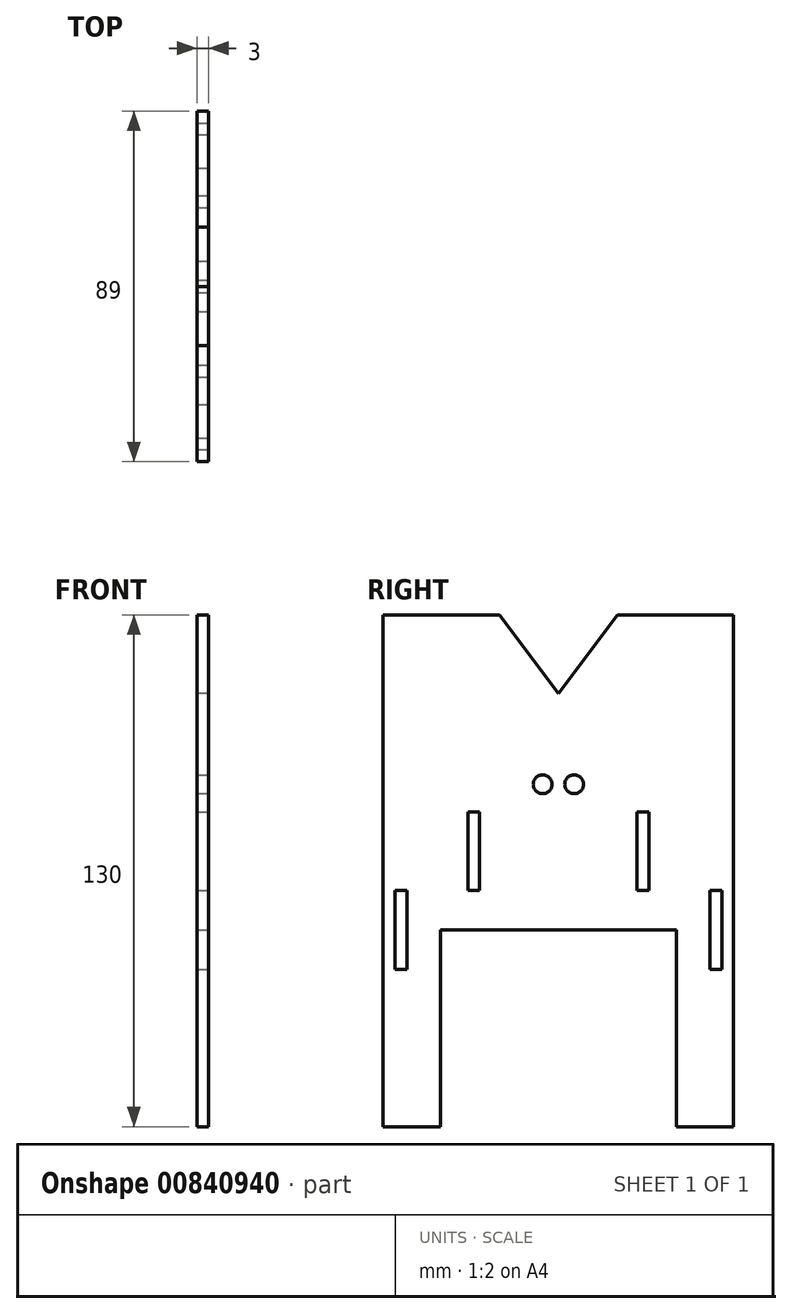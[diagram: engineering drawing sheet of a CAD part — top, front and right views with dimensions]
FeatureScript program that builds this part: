
annotation { "Feature Type Name" : "Feature", "Feature Type Description" : "" }
export const myFeature = defineFeature(function(context is Context, id is Id, definition is map)
    precondition{}
    {
        {
            var Q0;
            Q0=qCreatedBy(makeId("Right.planeOp"),FACE);
            var sketch = newSketch(context, id + "F0", { "sketchPlane" : qUnion([Q0])});
            skLineSegment(sketch, "E0", {"start": v(0, 130) * mm, "end": v(29.5, 130) * mm});
            skLineSegment(sketch, "E1", {"start": v(29.5, 130) * mm, "end": v(44.5, 110) * mm});
            skLineSegment(sketch, "E2", {"start": v(44.5, 110) * mm, "end": v(59.5, 130) * mm});
            skLineSegment(sketch, "E3", {"start": v(59.5, 130) * mm, "end": v(89, 130) * mm});
            skLineSegment(sketch, "E4", {"start": v(89, 130) * mm, "end": v(89, 0) * mm});
            skLineSegment(sketch, "E5", {"start": v(89, 0) * mm, "end": v(0, 0) * mm});
            skLineSegment(sketch, "E6", {"start": v(0, 0) * mm, "end": v(0, 130) * mm});
            skSolve(sketch);
        }
        {
            var Q0;
            Q0 = qSketchRegion(id + "F0", true);
            extrude(context, id + "F1", {"entities" : qUnion([Q0]), "depth" : 3 * mm, "offsetDistance" : 25 * mm});
        }
        {
            var Q0;
            Q0=makeQuery(id+"F1.opExtrude","CAP_FACE",FACE,{"disambiguationData":[OSD([sQuery(id+"F0.wireOp",EDGE,"E0"),sQuery(id+"F0.wireOp",EDGE,"E1"),sQuery(id+"F0.wireOp",EDGE,"E2"),sQuery(id+"F0.wireOp",EDGE,"E3"),sQuery(id+"F0.wireOp",EDGE,"E4"),sQuery(id+"F0.wireOp",EDGE,"E5"),sQuery(id+"F0.wireOp",EDGE,"E6")])],"isStart":false});
            var sketch = newSketch(context, id + "F2", { "sketchPlane" : qUnion([Q0])});
            skLineSegment(sketch, "E7.bottom", {"start": v(3, 60) * mm, "end": v(6, 60) * mm});
            skLineSegment(sketch, "E7.top", {"start": v(3, 40) * mm, "end": v(6, 40) * mm});
            skLineSegment(sketch, "E7.left", {"start": v(3, 60) * mm, "end": v(3, 40) * mm});
            skLineSegment(sketch, "E7.right", {"start": v(6, 60) * mm, "end": v(6, 40) * mm});
            skLineSegment(sketch, "E8", {"start": v(44.5, 110) * mm, "end": v(44.5, 73.4) * mm, "construction": true});
            skLineSegment(sketch, "E9.MirrorCS", {"start": v(83, 60) * mm, "end": v(83, 40) * mm});
            skLineSegment(sketch, "E10.MirrorCS", {"start": v(86, 60) * mm, "end": v(83, 60) * mm});
            skLineSegment(sketch, "E11.MirrorCS", {"start": v(86, 40) * mm, "end": v(83, 40) * mm});
            skLineSegment(sketch, "E12.MirrorCS", {"start": v(86, 60) * mm, "end": v(86, 40) * mm});
            skCircle(sketch, "E13", {"center": v(40.5, 87) * mm, "radius": 2.4 * mm});
            skCircle(sketch, "E14.MirrorC", {"center": v(48.5, 87) * mm, "radius": 2.4 * mm});
            skLineSegment(sketch, "E15.bottom", {"start": v(21.5, 80) * mm, "end": v(24.5, 80) * mm});
            skLineSegment(sketch, "E15.top", {"start": v(21.5, 60) * mm, "end": v(24.5, 60) * mm});
            skLineSegment(sketch, "E15.left", {"start": v(21.5, 80) * mm, "end": v(21.5, 60) * mm});
            skLineSegment(sketch, "E15.right", {"start": v(24.5, 80) * mm, "end": v(24.5, 60) * mm});
            skLineSegment(sketch, "E16.MirrorCS", {"start": v(67.5, 80) * mm, "end": v(64.5, 80) * mm});
            skLineSegment(sketch, "E17.MirrorCS", {"start": v(67.5, 60) * mm, "end": v(64.5, 60) * mm});
            skLineSegment(sketch, "E18.MirrorCS", {"start": v(64.5, 80) * mm, "end": v(64.5, 60) * mm});
            skLineSegment(sketch, "E19.MirrorCS", {"start": v(67.5, 80) * mm, "end": v(67.5, 60) * mm});
            skLineSegment(sketch, "E20.bottom", {"start": v(14.5, 0) * mm, "end": v(74.5, 0) * mm});
            skLineSegment(sketch, "E20.top", {"start": v(14.5, 50) * mm, "end": v(74.5, 50) * mm});
            skLineSegment(sketch, "E20.left", {"start": v(14.5, 0) * mm, "end": v(14.5, 50) * mm});
            skLineSegment(sketch, "E20.right", {"start": v(74.5, 0) * mm, "end": v(74.5, 50) * mm});
            skSolve(sketch);
        }
        {
            var Q0;
            Q0 = qSketchRegion(id + "F2", true);
            extrude(context, id + "F3", {"entities" : qUnion([Q0]), "operationType" : NewBodyOperationType.REMOVE, "oppositeDirection" : true, "depth" : 25 * mm, "offsetDistance" : 25 * mm});
        }
    });
